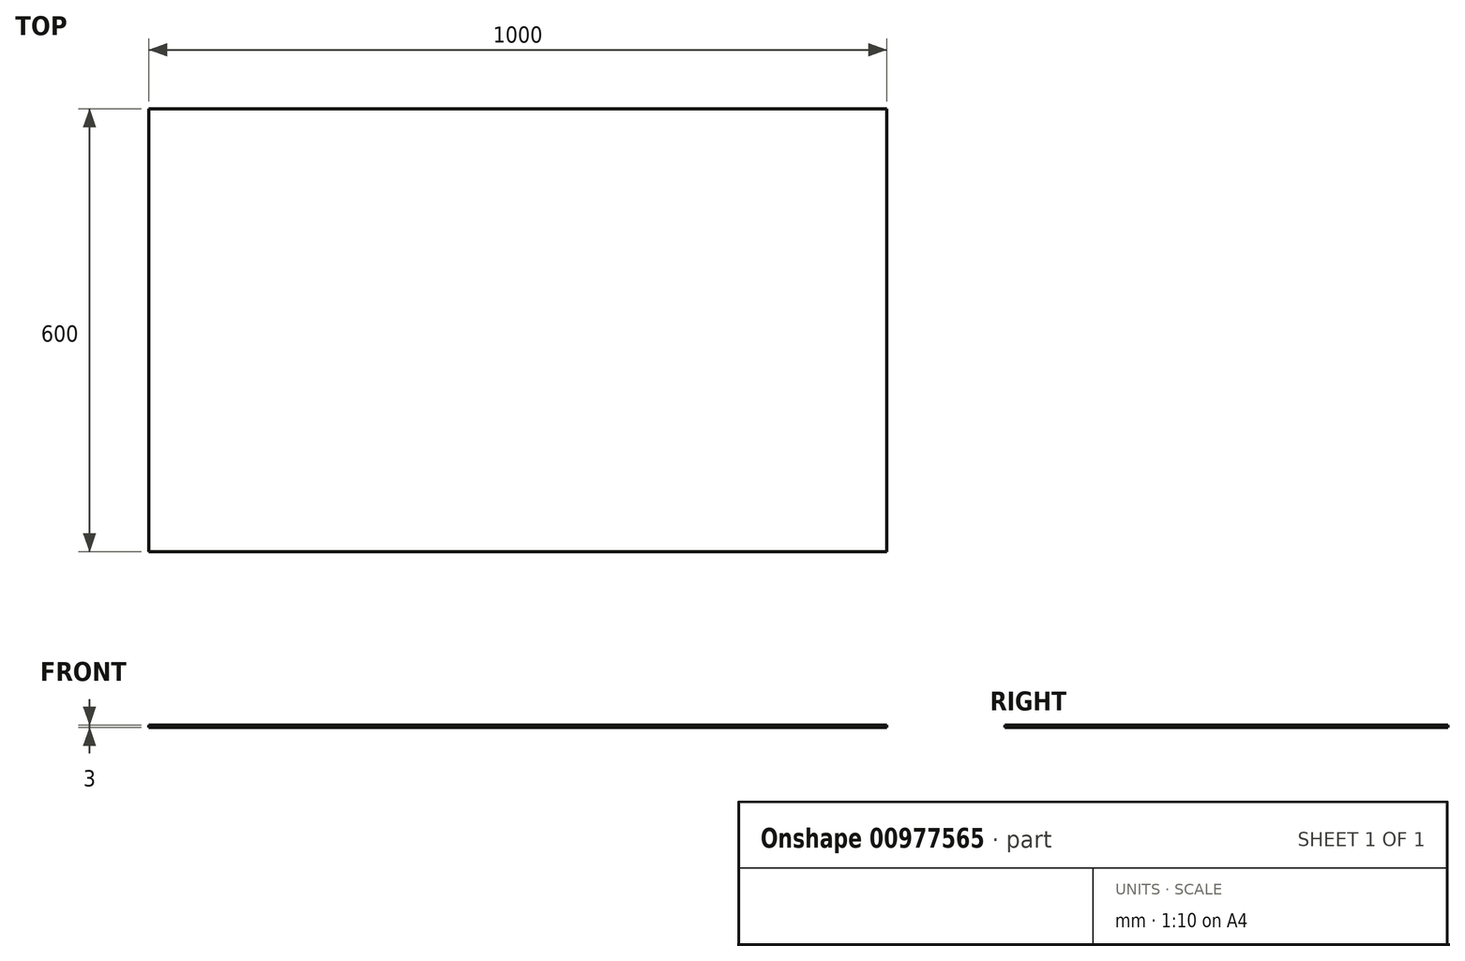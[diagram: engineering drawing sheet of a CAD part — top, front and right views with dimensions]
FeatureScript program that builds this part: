
annotation { "Feature Type Name" : "Feature", "Feature Type Description" : "" }
export const myFeature = defineFeature(function(context is Context, id is Id, definition is map)
    precondition{}
    {
        {
            var Q0;
            Q0=qCreatedBy(makeId("Top.planeOp"),FACE);
            var sketch = newSketch(context, id + "F0", { "sketchPlane" : qUnion([Q0])});
            skLineSegment(sketch, "E0.bottom", {"start": v(-500, 300) * mm, "end": v(500, 300) * mm});
            skLineSegment(sketch, "E0.top", {"start": v(-500, -300) * mm, "end": v(500, -300) * mm});
            skLineSegment(sketch, "E0.left", {"start": v(-500, 300) * mm, "end": v(-500, -300) * mm});
            skLineSegment(sketch, "E0.right", {"start": v(500, 300) * mm, "end": v(500, -300) * mm});
            skPoint(sketch, "E0.middle", {"position": v(0, 0) * mm});
            skSolve(sketch);
        }
        {
            var Q0;
            Q0 = qSketchRegion(id + "F0", true);
            var Q1;
            Q1=makeQuery(id+"F0.imprint","IMPRINT",FACE,{"disambiguationData":[TD([[makeQuery(id+"F0.imprint","IMPRINT",EDGE,{"derivedFrom":sQuery(id+"F0.wireOp",EDGE,"E0.bottom")}),-1.0]])]});
            extrude(context, id + "F1", {"entities" : qUnion([Q0, Q1]), "oppositeDirection" : true, "depth" : 3 * mm, "offsetDistance" : 25.4 * mm});
        }
    });
